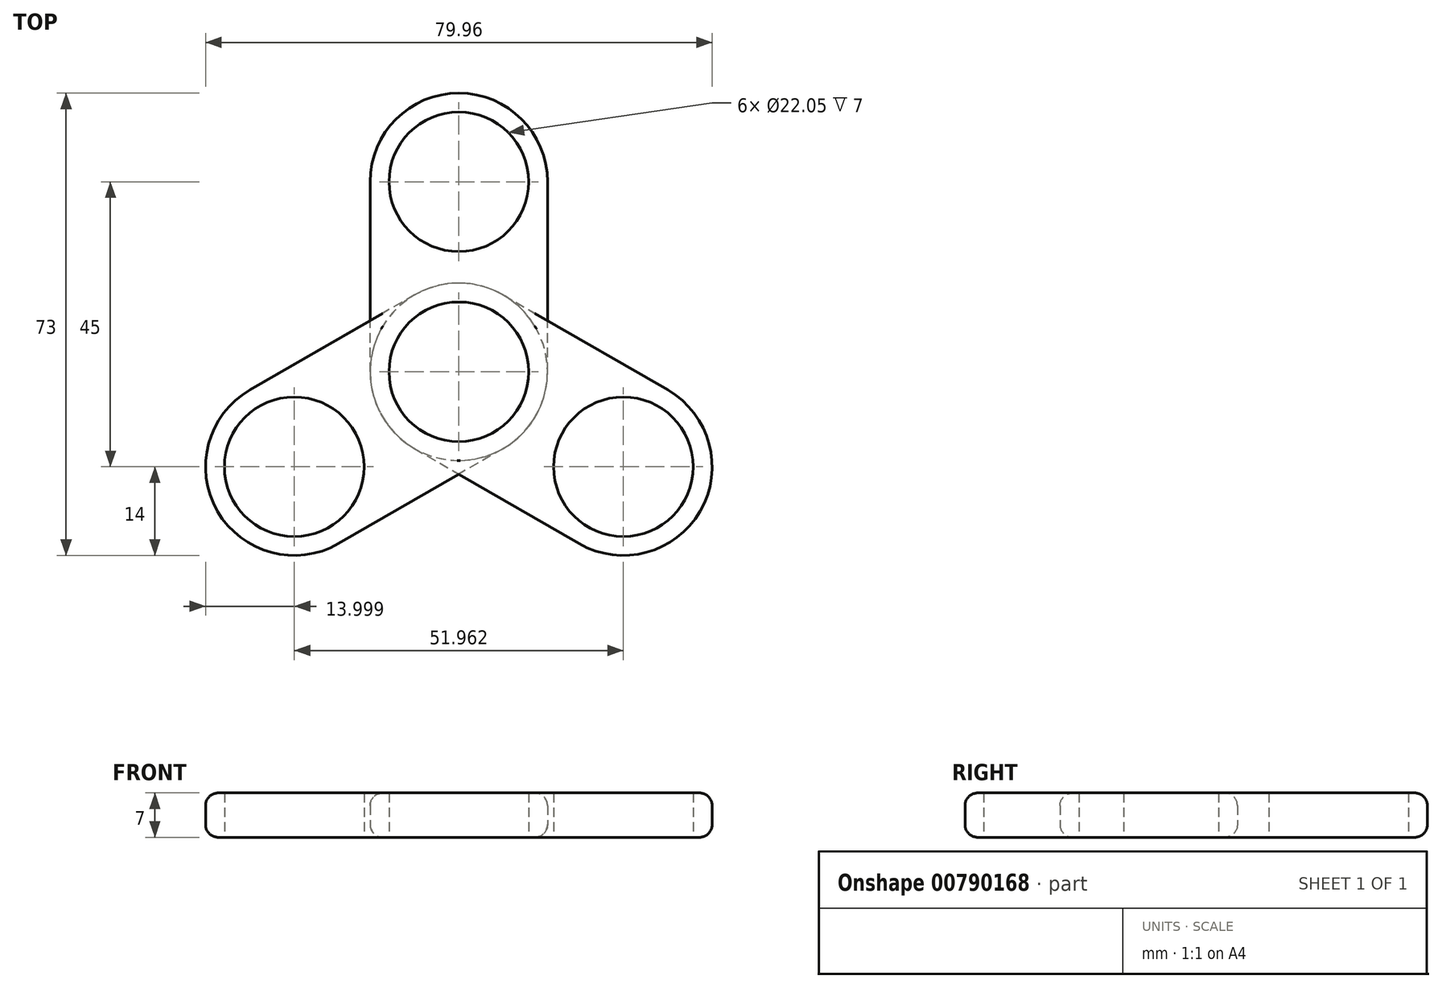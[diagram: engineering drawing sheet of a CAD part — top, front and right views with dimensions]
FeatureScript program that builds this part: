
annotation { "Feature Type Name" : "Feature", "Feature Type Description" : "" }
export const myFeature = defineFeature(function(context is Context, id is Id, definition is map)
    precondition{}
    {
        {
            var Q0;
            Q0=qCreatedBy(makeId("Top.planeOp"),FACE);
            var sketch = newSketch(context, id + "F0", { "sketchPlane" : qUnion([Q0])});
            skLineSegment(sketch, "E0.bottom", {"start": v(14, -15) * mm, "end": v(-14, -15) * mm});
            skLineSegment(sketch, "E0.top", {"start": v(14, 15) * mm, "end": v(-14, 15) * mm});
            skLineSegment(sketch, "E0.left", {"start": v(14, -15) * mm, "end": v(14, 15) * mm});
            skLineSegment(sketch, "E0.right", {"start": v(-14, -15) * mm, "end": v(-14, 15) * mm});
            skPoint(sketch, "E0.middle", {"position": v(0, 0) * mm});
            skCircle(sketch, "E1", {"center": v(0, 15) * mm, "radius": 14 * mm});
            skCircle(sketch, "E2", {"center": v(0, -15) * mm, "radius": 14 * mm});
            skCircle(sketch, "E3", {"center": v(0, -15) * mm, "radius": 11.03 * mm});
            skCircle(sketch, "E4", {"center": v(0, 15) * mm, "radius": 11.03 * mm});
            skSolve(sketch);
        }
        {
            var Q0;
            {var subQ1=sQuery(id+"F0.wireOp",EDGE,"E0.top");var subQ3=sQuery(id+"F0.wireOp",EDGE,"E4");var subQ4=makeQuery(id+"F0.imprint","INTERSECT",VERTEX,{"disambiguationData":[OD(0.0)],"derivedFrom":[subQ1,subQ3]});Q0=makeQuery(id+"F0.imprint","IMPRINT",FACE,{"disambiguationData":[TD([[makeQuery(id+"F0.imprint","IMPRINT",EDGE,{"disambiguationData":[TD([[subQ4,-1.0]])],"derivedFrom":subQ3}),-1.0]])]});}
            var Q1;
            {var subQ1=sQuery(id+"F0.wireOp",EDGE,"E0.top");var subQ3=sQuery(id+"F0.wireOp",EDGE,"E4");var subQ4=makeQuery(id+"F0.imprint","INTERSECT",VERTEX,{"disambiguationData":[OD(0.0)],"derivedFrom":[subQ1,subQ3]});Q1=makeQuery(id+"F0.imprint","IMPRINT",FACE,{"disambiguationData":[TD([[makeQuery(id+"F0.imprint","IMPRINT",EDGE,{"disambiguationData":[TD([[subQ4,1.0]])],"derivedFrom":subQ3}),-1.0]])]});}
            var Q2;
            {var subQ0=sQuery(id+"F0.wireOp",EDGE,"E0.left");Q2=makeQuery(id+"F0.imprint","IMPRINT",FACE,{"disambiguationData":[TD([[makeQuery(id+"F0.imprint","IMPRINT",EDGE,{"derivedFrom":subQ0}),1.0]])]});}
            var Q3;
            {var subQ1=sQuery(id+"F0.wireOp",EDGE,"E0.bottom");var subQ3=sQuery(id+"F0.wireOp",EDGE,"E3");var subQ4=makeQuery(id+"F0.imprint","INTERSECT",VERTEX,{"disambiguationData":[OD(0.0)],"derivedFrom":[subQ1,subQ3]});Q3=makeQuery(id+"F0.imprint","IMPRINT",FACE,{"disambiguationData":[TD([[makeQuery(id+"F0.imprint","IMPRINT",EDGE,{"disambiguationData":[TD([[subQ4,-1.0]])],"derivedFrom":subQ3}),-1.0]])]});}
            var Q4;
            {var subQ1=sQuery(id+"F0.wireOp",EDGE,"E0.bottom");var subQ3=sQuery(id+"F0.wireOp",EDGE,"E3");var subQ4=makeQuery(id+"F0.imprint","INTERSECT",VERTEX,{"disambiguationData":[OD(0.0)],"derivedFrom":[subQ1,subQ3]});Q4=makeQuery(id+"F0.imprint","IMPRINT",FACE,{"disambiguationData":[TD([[makeQuery(id+"F0.imprint","IMPRINT",EDGE,{"disambiguationData":[TD([[subQ4,1.0]])],"derivedFrom":subQ3}),-1.0]])]});}
            extrude(context, id + "F1", {"entities" : qUnion([Q0, Q1, Q2, Q3, Q4]), "depth" : 7 * mm, "offsetDistance" : 25 * mm});
        }
        {
            var Q0;
            Q0=makeQuery(id+"F1.opExtrude","SWEPT_BODY",BODY,{"disambiguationData":[OSD([sQuery(id+"F0.wireOp",EDGE,"E0.left"),sQuery(id+"F0.wireOp",EDGE,"E0.right"),sQuery(id+"F0.wireOp",EDGE,"E1"),sQuery(id+"F0.wireOp",EDGE,"E2"),sQuery(id+"F0.wireOp",EDGE,"E3"),sQuery(id+"F0.wireOp",EDGE,"E4")])]});
            var Q1;
            Q1=makeQuery(id+"F1.opExtrude","CAP_EDGE",EDGE,{"disambiguationData":[OSD([sQuery(id+"F0.wireOp",EDGE,"E3")])],"isStart":false});
            circularPattern(context, id + "F2", {"entities" : qUnion([Q0]), "axis" : qUnion([Q1]), "angle" : 360 * degree, "instanceCount" : 3, "equalSpace" : true});
        }
        {
            var Q0;
            Q0=makeQuery(id+"F1.opExtrude","CAP_EDGE",EDGE,{"disambiguationData":[OSD([sQuery(id+"F0.wireOp",EDGE,"E0.right")])],"isStart":false});
            var Q1;
            Q1=makeQuery(id+"F2.opPattern","COPY",EDGE,{"derivedFrom":makeQuery(id+"F1.opExtrude","CAP_EDGE",EDGE,{"disambiguationData":[OSD([sQuery(id+"F0.wireOp",EDGE,"E0.left")])],"isStart":false}),"instanceName":"1"});
            var Q2;
            Q2=makeQuery(id+"F2.opPattern","COPY",EDGE,{"derivedFrom":makeQuery(id+"F1.opExtrude","CAP_EDGE",EDGE,{"disambiguationData":[OSD([sQuery(id+"F0.wireOp",EDGE,"E0.left")])],"isStart":false}),"instanceName":"2"});
            var Q3;
            Q3=makeQuery(id+"F2.opPattern","COPY",EDGE,{"derivedFrom":makeQuery(id+"F1.opExtrude","CAP_EDGE",EDGE,{"disambiguationData":[OSD([sQuery(id+"F0.wireOp",EDGE,"E0.right")])],"isStart":true}),"instanceName":"1"});
            var Q4;
            Q4=makeQuery(id+"F2.opPattern","COPY",EDGE,{"derivedFrom":makeQuery(id+"F1.opExtrude","CAP_EDGE",EDGE,{"disambiguationData":[OSD([sQuery(id+"F0.wireOp",EDGE,"E0.left")])],"isStart":true}),"instanceName":"2"});
            var Q5;
            Q5=makeQuery(id+"F1.opExtrude","CAP_EDGE",EDGE,{"disambiguationData":[OSD([sQuery(id+"F0.wireOp",EDGE,"E0.left")])],"isStart":true});
            fillet(context, id + "F3", {"entities" : qUnion([Q0, Q1, Q2, Q3, Q4, Q5]), "radius" : 2 * mm, "tangentPropagation" : true, "allowEdgeOverflow" : false});
        }
    });
